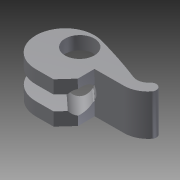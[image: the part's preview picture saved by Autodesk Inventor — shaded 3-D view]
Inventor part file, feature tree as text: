
AUTODESK INVENTOR PART (.ipt)
format: ipt  version: 2012 (Build 160160000, 160)  size: 167,936 bytes
history: native  units: mm
features: extrude x4, sketch x3, hole x2, plane x1
ambient origin geometry x8: Origin, YZ Plane, XZ Plane, XY Plane, X Axis, Y Axis, Z Axis, Center Point
bodies: Solid1 (feature_tree)
feature tree (10):
  extrude  "Extrusion1"  Depth=10.0mm
  hole  "Hole1"  [1 undecoded]
  extrude  "Extrusion2"  Depth=4.958682mm
  plane  "Work Plane1"
  sketch  "Sketch3"  dims[d6=159.013839mm d7=4.958682mm d8=4.189042mm d9=7.87754mm d10=0.487189mm d11=10.0mm d12=14.0mm d13=0.0mm d15=9.0mm d16=14.0mm d17=10.0mm d18=6.0mm d19=4.0mm d20=2.0mm d21=90.0deg d22=8.0mm d23=20.594885mm d24=14.0mm d25=0.0mm d26=0.0mm d27=5.0mm d28=20.0mm d29=14.0mm d30=0.0mm d31=8.0mm d32=3.5mm d33=14.0mm d34=0.0mm d46=10.0mm d47=10.0mm d37=5.0mm d38=6.0mm d39=4.0mm d40=2.0mm d41=90.0deg d42=8.0mm d43=20.594885mm]
  extrude  "Extrusion3"  Depth=4.189042mm
  extrude  "Extrusion4"  Depth=7.87754mm
  hole  "Hole2"  [1 undecoded]
  sketch  "Sketch1"  dims[d2=10.0mm d3=10.0mm]
  sketch  "Sketch2"  dims[d4=8.279418mm d5=10.072992mm]
note: 2 required parameter values undecoded (feature->parameter linkage not recoverable at this tier; creation-order binding heuristic only, values carry confidence <= 0.55)
